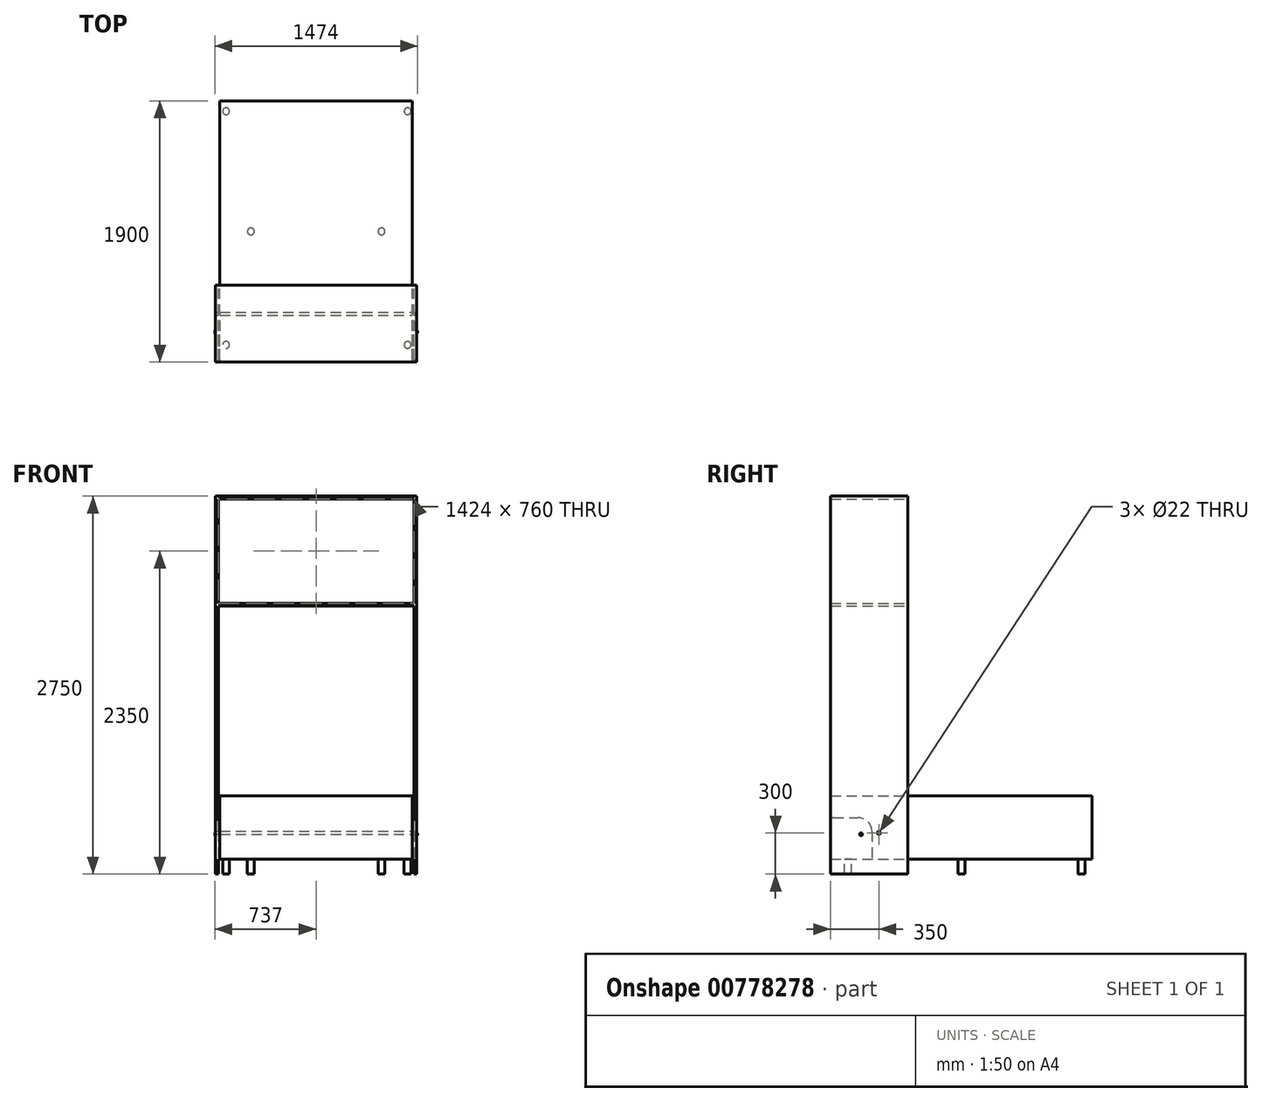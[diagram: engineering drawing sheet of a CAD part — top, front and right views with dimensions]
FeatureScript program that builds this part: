
annotation { "Feature Type Name" : "Feature", "Feature Type Description" : "" }
export const myFeature = defineFeature(function(context is Context, id is Id, definition is map)
    precondition{}
    {
        {
            var Q0;
            Q0=qCreatedBy(makeId("Top.planeOp"),FACE);
            var sketch = newSketch(context, id + "F0", { "sketchPlane" : qUnion([Q0])});
            skLineSegment(sketch, "E0.bottom", {"start": v(0, 0) * mm, "end": v(1400, 0) * mm});
            skLineSegment(sketch, "E0.top", {"start": v(0, 1900) * mm, "end": v(1400, 1900) * mm});
            skLineSegment(sketch, "E0.left", {"start": v(0, 0) * mm, "end": v(0, 1900) * mm});
            skLineSegment(sketch, "E0.right", {"start": v(1400, 0) * mm, "end": v(1400, 1900) * mm});
            skSolve(sketch);
        }
        {
            var Q0;
            Q0 = qSketchRegion(id + "F0", true);
            extrude(context, id + "F1", {"entities" : qUnion([Q0]), "depth" : 460 * mm, "offsetDistance" : 25 * mm});
        }
        {
            var Q0;
            Q0=makeQuery(id+"F1.opExtrude","CAP_FACE",FACE,{"disambiguationData":[OSD([sQuery(id+"F0.wireOp",EDGE,"E0.bottom"),sQuery(id+"F0.wireOp",EDGE,"E0.top"),sQuery(id+"F0.wireOp",EDGE,"E0.left"),sQuery(id+"F0.wireOp",EDGE,"E0.right")])],"isStart":true});
            var sketch = newSketch(context, id + "F2", { "sketchPlane" : qUnion([Q0])});
            skCircle(sketch, "E1", {"center": v(45, -125) * mm, "radius": 25 * mm});
            skCircle(sketch, "E2.0.1.0", {"center": v(45, -1825) * mm, "radius": 25 * mm});
            skCircle(sketch, "E2.1.0.0", {"center": v(1365, -125) * mm, "radius": 25 * mm});
            skCircle(sketch, "E2.1.1.0", {"center": v(1365, -1825) * mm, "radius": 25 * mm});
            skLineSegment(sketch, "E2.direction1", {"start": v(45, -125) * mm, "end": v(1365, -125) * mm, "construction": true});
            skLineSegment(sketch, "E2.direction2", {"start": v(45, -125) * mm, "end": v(45, -1825) * mm, "construction": true});
            skCircle(sketch, "E3", {"center": v(225, -950) * mm, "radius": 25 * mm});
            skPoint(sketch, "E3.centerSnap0", {"position": v(0, -950) * mm});
            skLineSegment(sketch, "E4", {"start": v(700, 0) * mm, "end": v(700, -1900) * mm, "construction": true});
            skCircle(sketch, "E5.MirrorC", {"center": v(1175, -950) * mm, "radius": 25 * mm});
            skSolve(sketch);
        }
        {
            var Q0;
            Q0 = qSketchRegion(id + "F2", true);
            extrude(context, id + "F3", {"entities" : qUnion([Q0]), "operationType" : NewBodyOperationType.ADD, "depth" : 110 * mm, "offsetDistance" : 25 * mm});
        }
        {
            var Q0;
            Q0=makeQuery(id+"F1.opExtrude","SWEPT_FACE",FACE,{"disambiguationData":[OSD([sQuery(id+"F0.wireOp",EDGE,"E0.right")])]});
            var sketch = newSketch(context, id + "F4", { "sketchPlane" : qUnion([Q0])});
            skLineSegment(sketch, "E6.bottom", {"start": v(20, 300) * mm, "end": v(200, 300) * mm});
            skLineSegment(sketch, "E6.top", {"start": v(0, 0) * mm, "end": v(300, 0) * mm});
            skLineSegment(sketch, "E6.left", {"start": v(0, 280) * mm, "end": v(0, 0) * mm});
            skLineSegment(sketch, "E6.right", {"start": v(300, 200) * mm, "end": v(300, 0) * mm});
            skPoint(sketch, "E7.visualSharp", {"position": v(0, 460) * mm});
            skArc(sketch, "E7.filletArc", {"start": v(20, 300) * mm, "mid": v(5.86, 294.14) * mm, "end": v(0, 280) * mm});
            skPoint(sketch, "E8.visualSharp", {"position": v(300, 300) * mm});
            skArc(sketch, "E8.filletArc", {"start": v(300, 200) * mm, "mid": v(270.71, 270.71) * mm, "end": v(200, 300) * mm});
            skSolve(sketch);
        }
        {
            var Q0;
            Q0 = qSketchRegion(id + "F4", true);
            extrude(context, id + "F5", {"entities" : qUnion([Q0]), "depth" : 12 * mm, "offsetDistance" : 25 * mm});
        }
        {
            var Q0;
            Q0=makeQuery(id+"F5.opExtrude","CAP_FACE",FACE,{"disambiguationData":[OSD([sQuery(id+"F4.wireOp",EDGE,"E6.bottom"),sQuery(id+"F4.wireOp",EDGE,"E6.top"),sQuery(id+"F4.wireOp",EDGE,"E6.left"),sQuery(id+"F4.wireOp",EDGE,"E6.right"),sQuery(id+"F4.wireOp",EDGE,"E7.filletArc"),sQuery(id+"F4.wireOp",EDGE,"E8.filletArc")])],"isStart":false});
            var sketch = newSketch(context, id + "F6", { "sketchPlane" : qUnion([Q0])});
            skCircle(sketch, "E9", {"center": v(220, 180) * mm, "radius": 10 * mm});
            skPoint(sketch, "E9.centerSnap0", {"position": v(-60, 180) * mm});
            skPoint(sketch, "E9.centerSnap1", {"position": v(220, -5) * mm});
            skSolve(sketch);
        }
        {
            var Q0;
            Q0 = qSketchRegion(id + "F6", true);
            extrude(context, id + "F7", {"entities" : qUnion([Q0]), "operationType" : NewBodyOperationType.ADD, "depth" : 25 * mm, "offsetDistance" : 25 * mm});
        }
        {
            var Q0;
            Q0=qCreatedBy(makeId("Right.planeOp"),FACE);
            cPlane(context, id + "F8", {"entities" : qUnion([Q0]), "cplaneType" : CPlaneType.OFFSET, "offset" : (1400 / 2) * mm, "width" : 150 * mm, "height" : 150 * mm});
        }
        {
            var Q0;
            Q0=makeQuery(id+"F5.opExtrude","SWEPT_BODY",BODY,{"disambiguationData":[OSD([sQuery(id+"F4.wireOp",EDGE,"E6.bottom"),sQuery(id+"F4.wireOp",EDGE,"E6.top"),sQuery(id+"F4.wireOp",EDGE,"E6.left"),sQuery(id+"F4.wireOp",EDGE,"E6.right"),sQuery(id+"F4.wireOp",EDGE,"E7.filletArc"),sQuery(id+"F4.wireOp",EDGE,"E8.filletArc")])]});
            var Q1;
            Q1=qCreatedBy(id+"F8.planeOp",FACE);
            mirror(context, id + "F9", {"entities" : qUnion([Q0]), "mirrorPlane" : qUnion([Q1])});
        }
        {
            var Q0;
            Q0=makeQuery(id+"F5.opExtrude","CAP_FACE",FACE,{"disambiguationData":[OSD([sQuery(id+"F4.wireOp",EDGE,"E6.bottom"),sQuery(id+"F4.wireOp",EDGE,"E6.top"),sQuery(id+"F4.wireOp",EDGE,"E6.left"),sQuery(id+"F4.wireOp",EDGE,"E6.right"),sQuery(id+"F4.wireOp",EDGE,"E7.filletArc"),sQuery(id+"F4.wireOp",EDGE,"E8.filletArc")])],"isStart":false});
            var sketch = newSketch(context, id + "F10", { "sketchPlane" : qUnion([Q0])});
            skLineSegment(sketch, "E10.bottom", {"start": v(0, -110) * mm, "end": v(560, -110) * mm});
            skLineSegment(sketch, "E10.top", {"start": v(0, 2640) * mm, "end": v(560, 2640) * mm});
            skLineSegment(sketch, "E10.left", {"start": v(0, -110) * mm, "end": v(0, 2640) * mm});
            skLineSegment(sketch, "E10.right", {"start": v(560, -110) * mm, "end": v(560, 2640) * mm});
            skSolve(sketch);
        }
        {
            var Q0;
            Q0 = qSketchRegion(id + "F10", true);
            extrude(context, id + "F11", {"entities" : qUnion([Q0]), "depth" : 20 * mm, "offsetDistance" : 25 * mm});
        }
        {
            var Q0;
            Q0=makeQuery(id+"F11.opExtrude","CAP_FACE",FACE,{"disambiguationData":[OSD([sQuery(id+"F10.wireOp",EDGE,"E10.bottom"),sQuery(id+"F10.wireOp",EDGE,"E10.top"),sQuery(id+"F10.wireOp",EDGE,"E10.left"),sQuery(id+"F10.wireOp",EDGE,"E10.right")])],"isStart":true});
            var sketch = newSketch(context, id + "F12", { "sketchPlane" : qUnion([Q0])});
            skLineSegment(sketch, "E11.bottom", {"start": v(0, 2640) * mm, "end": v(-560, 2640) * mm});
            skLineSegment(sketch, "E11.top", {"start": v(0, 2620) * mm, "end": v(-560, 2620) * mm});
            skLineSegment(sketch, "E11.left", {"start": v(0, 2640) * mm, "end": v(0, 2620) * mm});
            skLineSegment(sketch, "E11.right", {"start": v(-560, 2640) * mm, "end": v(-560, 2620) * mm});
            skLineSegment(sketch, "E12.bottom", {"start": v(0, 1860) * mm, "end": v(-560, 1860) * mm});
            skLineSegment(sketch, "E12.top", {"start": v(0, 1840) * mm, "end": v(-560, 1840) * mm});
            skLineSegment(sketch, "E12.left", {"start": v(0, 1860) * mm, "end": v(0, 1840) * mm});
            skLineSegment(sketch, "E12.right", {"start": v(-560, 1860) * mm, "end": v(-560, 1840) * mm});
            skSolve(sketch);
        }
        {
            var Q0;
            Q0 = qSketchRegion(id + "F12", true);
            extrude(context, id + "F13", {"entities" : qUnion([Q0]), "operationType" : NewBodyOperationType.ADD, "depth" : (1400 + 40) * mm, "offsetDistance" : 25 * mm});
        }
        {
            var Q0;
            Q0=makeQuery(id+"F11.opExtrude","SWEPT_BODY",BODY,{"disambiguationData":[OSD([sQuery(id+"F10.wireOp",EDGE,"E10.bottom"),sQuery(id+"F10.wireOp",EDGE,"E10.top"),sQuery(id+"F10.wireOp",EDGE,"E10.left"),sQuery(id+"F10.wireOp",EDGE,"E10.right")])]});
            var Q1;
            Q1=qCreatedBy(id+"F8.planeOp",FACE);
            mirror(context, id + "F14", {"operationType" : NewBodyOperationType.ADD, "entities" : qUnion([Q0]), "mirrorPlane" : qUnion([Q1])});
        }
        {
            var Q0;
            Q0=makeQuery(id+"F11.opExtrude","CAP_FACE",FACE,{"disambiguationData":[OSD([sQuery(id+"F10.wireOp",EDGE,"E10.bottom"),sQuery(id+"F10.wireOp",EDGE,"E10.top"),sQuery(id+"F10.wireOp",EDGE,"E10.left"),sQuery(id+"F10.wireOp",EDGE,"E10.right")])],"isStart":false});
            var sketch = newSketch(context, id + "F15", { "sketchPlane" : qUnion([Q0])});
            skCircle(sketch, "E13", {"center": v(350, 190) * mm, "radius": 11 * mm});
            skLineSegment(sketch, "E14", {"start": v(0, 293.05) * mm, "end": v(403.05, -110) * mm, "construction": true});
            skLineSegment(sketch, "E15", {"start": v(0, 293.05) * mm, "end": v(403.05, 696.1) * mm, "construction": true});
            skLineSegment(sketch, "E16", {"start": v(403.05, 696.1) * mm, "end": v(806.1, 293.05) * mm, "construction": true});
            skLineSegment(sketch, "E17", {"start": v(806.1, 293.05) * mm, "end": v(403.05, -110) * mm, "construction": true});
            skLineSegment(sketch, "E18", {"start": v(604.58, 494.58) * mm, "end": v(201.53, 91.53) * mm, "construction": true});
            skLineSegment(sketch, "E19", {"start": v(201.53, 494.58) * mm, "end": v(604.58, 91.53) * mm, "construction": true});
            skSolve(sketch);
        }
        {
            var Q0;
            Q0 = qSketchRegion(id + "F15", true);
            extrude(context, id + "F16", {"entities" : qUnion([Q0]), "operationType" : NewBodyOperationType.REMOVE, "endBound" : BoundingType.THROUGH_ALL, "oppositeDirection" : true, "depth" : 25 * mm, "offsetDistance" : 25 * mm});
        }
    });
